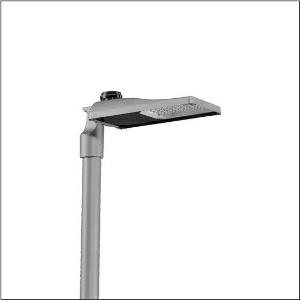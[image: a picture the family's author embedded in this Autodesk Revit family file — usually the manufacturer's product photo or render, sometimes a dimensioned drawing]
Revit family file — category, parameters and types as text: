
# Revit family: streetlight_sl_31_mini___st1_0a_5xh2d35n08ha_d2d6
name_source: partatom
category: Lighting Fixtures
units: mm (PartAtom-declared; Revit-internal decimal feet)

## family parameters
Cut with Voids When Loaded = No
Host = Face
Light Source = No
Part Type = Normal
Room Calculation Point = No
Round Connector Dimension = Use Diameter
Shared = No

## types (1)
- --- (1 x LED, 9240 lm, 68.3 W, 3000K)
    Apparent Load = 68 VA
    CIE Flux Codes = 37 72 97 100 100
    Color Rendering = 70
    Color Temperature = 3000K
    Default Elevation = 1800 mm
    Description = Streetlight SL 31 mini NEMA (7pin), Desk-Remote mast luminaire for post-top, side-entry; light control with lens of PMMA; light distribution: ST1.0a, direct asymmetric distribution, for standard-compliant lighting for roads and squares; LED: luminous flux: 9.240lm, light colour: 730, colour temperature: 3000K; luminous efficacy: 135,3lm/W; control: pre-setting: linear dimming characteristic, flexible luminous flux parameterisation, time-dependent luminous flux control, constant luminous flux control, intelligent temperature release in ECG and LED module, overheat protection; luminaire housing, of diecast aluminium, Siteco® metallic grey (DB 702S), corrosivity category C5 high according to DIN EN ISO 12944; cover of toughened safety glass, transparent, mast flange of diecast aluminium, Siteco® metallic grey (DB 702S), spigot size: 76/60mm, mast flange included unmounted; with cable H07RN-F 3x 1.5mm², cable length: 8,5m, connection cable pre-assembled; mains connection: 220..240V, AC, 50/60Hz; power consumption (at start of service life): 68,3W / (at end of service life): 74,8W / (with reduced operation 50%): 29,7W; protection rating (complete): IP66; insulation class (complete): insulation class I (protective earthing); impact resistance: IK10; certification: CE, ENEC, ENEC+, VDE, UKCA; permissible operating ambient temperature for outdoor applications: -40..+50°C; packaging unit: 1 piece

Light Distribution: ST1.0a
    Height = 76 mm
    Lamp = 1 x LED
    Lamp Light Flux = 9240 lm
    Lamp Power = 68.3 W
    Lamp count = 1
    Length = 547 mm
    Luminous efficacy = 135 lm/W
    Manufacturer = Siteco
    ModVariant = No
    Model = 5XH2D35N08HA
    Number of Poles = 1
    OnlyDefault = Yes
    Power Factor = 1
    Product Name = Streetlight SL 31 mini | ST1.0a
    Product group = mast luminaire | pylon top
    ProductGroupID = 6100
    Protection Class = Protection class I
    Protection Degree = IP 66
    RLX_Detail_Level = 1
    RLX_Emergency_Light_Flux = 0 lm
    RLX_Emergency_Type = 0
    RLX_Emergency_Type_DB = No
    RlxData = <blob elided: 40145 chars, md5=7481e11f>
    Socket = socket
    Standby Power = 0 W
    System Light Flux = 9240 lm
    System Power = 68 W
    Type Comments = factory setting: luminous flux: 100 % | dim-lin: 254 | 693 mA
    Type Image = l_1300322.jpg
    URL = http://relux.com
    VarID = @adj_054546
    Voltage = 0 V
    Weight = 0.00 kg
    Width = 265 mm

## geometry (parser evidence)
native form markers: Blend x4, Sweep x11
no freeform markers — native parametric forms only
